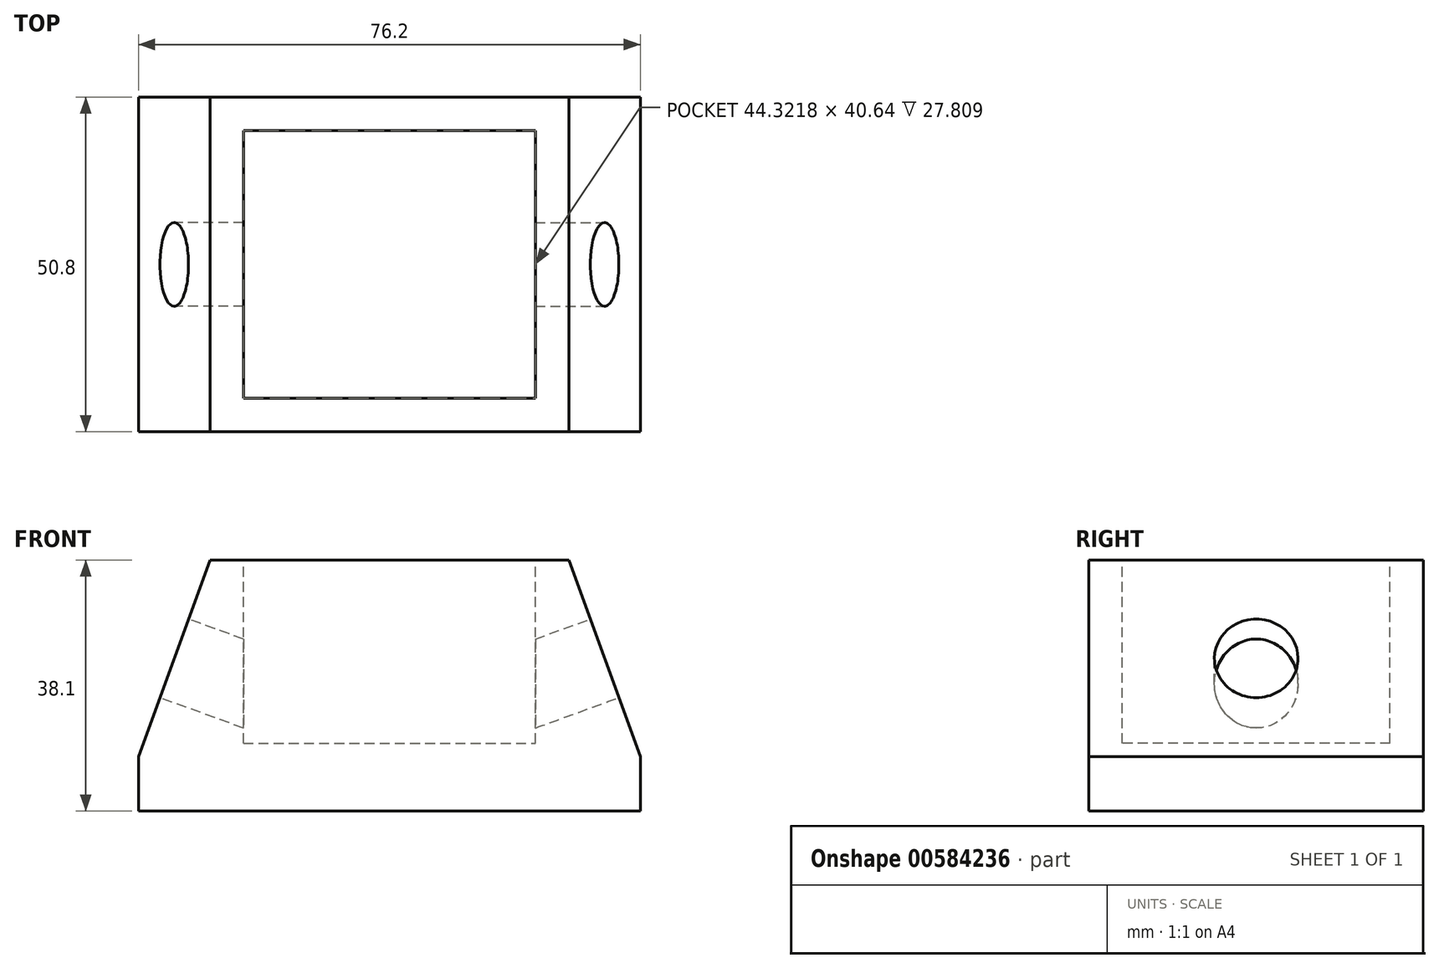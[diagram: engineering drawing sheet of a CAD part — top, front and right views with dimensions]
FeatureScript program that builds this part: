
annotation { "Feature Type Name" : "Feature", "Feature Type Description" : "" }
export const myFeature = defineFeature(function(context is Context, id is Id, definition is map)
    precondition{}
    {
        {
            var Q0;
            Q0=qCreatedBy(makeId("Top.planeOp"),FACE);
            var sketch = newSketch(context, id + "F0", { "sketchPlane" : qUnion([Q0])});
            skLineSegment(sketch, "E0.bottom", {"start": v(0, 0) * mm, "end": v(76.2, 0) * mm});
            skLineSegment(sketch, "E0.top", {"start": v(0, 50.8) * mm, "end": v(76.2, 50.8) * mm});
            skLineSegment(sketch, "E0.left", {"start": v(0, 0) * mm, "end": v(0, 50.8) * mm});
            skLineSegment(sketch, "E0.right", {"start": v(76.2, 0) * mm, "end": v(76.2, 50.8) * mm});
            skSolve(sketch);
        }
        {
            var Q0;
            Q0=makeQuery(id+"F0.imprint","IMPRINT",FACE,{"disambiguationData":[TD([[makeQuery(id+"F0.imprint","IMPRINT",EDGE,{"derivedFrom":sQuery(id+"F0.wireOp",EDGE,"E0.bottom")}),1.0]])]});
            extrude(context, id + "F1", {"entities" : qUnion([Q0]), "depth" : 38.1 * mm, "offsetDistance" : 25.4 * mm});
        }
        {
            var Q0;
            Q0=makeQuery(id+"F1.opExtrude","SWEPT_FACE",FACE,{"disambiguationData":[OSD([sQuery(id+"F0.wireOp",EDGE,"E0.bottom")])]});
            var sketch = newSketch(context, id + "F2", { "sketchPlane" : qUnion([Q0])});
            skLineSegment(sketch, "E1", {"start": v(0, 8.26) * mm, "end": v(10.86, 38.1) * mm});
            skLineSegment(sketch, "E2", {"start": v(38.1, 38.1) * mm, "end": v(38.1, 0) * mm, "construction": true});
            skLineSegment(sketch, "E3.MirrorCS", {"start": v(76.2, 8.26) * mm, "end": v(65.34, 38.1) * mm});
            skLineSegment(sketch, "E4", {"start": v(0, 11.3) * mm, "end": v(76.2, 11.3) * mm, "construction": true});
            skLineSegment(sketch, "E5", {"start": v(5.43, 23.18) * mm, "end": v(38.1, 11.3) * mm, "construction": true});
            skLineSegment(sketch, "E6", {"start": v(0, 10.3) * mm, "end": v(76.2, 10.3) * mm, "construction": true});
            skPoint(sketch, "E7", {"position": v(38.1, 10.3) * mm});
            skSolve(sketch);
        }
        {
            var Q0;
            {var subQ0=sQuery(id+"F2.wireOp",EDGE,"E1");Q0=makeQuery(id+"F2.imprint","IMPRINT",FACE,{"disambiguationData":[TD([[makeQuery(id+"F2.imprint","IMPRINT",EDGE,{"derivedFrom":subQ0}),1.0]])]});}
            var Q1;
            {var subQ0=sQuery(id+"F2.wireOp",EDGE,"E3.MirrorCS");Q1=makeQuery(id+"F2.imprint","IMPRINT",FACE,{"disambiguationData":[TD([[makeQuery(id+"F2.imprint","IMPRINT",EDGE,{"derivedFrom":subQ0}),-1.0]])]});}
            extrude(context, id + "F3", {"entities" : qUnion([Q0, Q1]), "operationType" : NewBodyOperationType.REMOVE, "endBound" : BoundingType.UP_TO_NEXT, "oppositeDirection" : true, "depth" : 25.4 * mm, "offsetDistance" : 25.4 * mm});
        }
        {
            var Q0;
            Q0=makeQuery(id+"F1.opExtrude","CAP_FACE",FACE,{"disambiguationData":[OSD([sQuery(id+"F0.wireOp",EDGE,"E0.bottom"),sQuery(id+"F0.wireOp",EDGE,"E0.top"),sQuery(id+"F0.wireOp",EDGE,"E0.left"),sQuery(id+"F0.wireOp",EDGE,"E0.right")])],"isStart":false});
            var sketch = newSketch(context, id + "F4", { "sketchPlane" : qUnion([Q0])});
            skLineSegment(sketch, "E8.0", {"start": v(15.94, 45.72) * mm, "end": v(15.94, 5.08) * mm});
            skLineSegment(sketch, "E8.1", {"start": v(15.94, 45.72) * mm, "end": v(60.26, 45.72) * mm});
            skLineSegment(sketch, "E8.2", {"start": v(60.26, 45.72) * mm, "end": v(60.26, 5.08) * mm});
            skLineSegment(sketch, "E8.3", {"start": v(15.94, 5.08) * mm, "end": v(60.26, 5.08) * mm});
            skSolve(sketch);
        }
        {
            var Q0;
            Q0=makeQuery(id+"F4.imprint","IMPRINT",FACE,{"disambiguationData":[TD([[makeQuery(id+"F4.imprint","IMPRINT",EDGE,{"derivedFrom":sQuery(id+"F4.wireOp",EDGE,"E8.0")}),1.0]])]});
            var Q1;
            Q1=sQuery(id+"F2.wireOp",VERTEX,"E7");
            extrude(context, id + "F5", {"entities" : qUnion([Q0]), "operationType" : NewBodyOperationType.REMOVE, "endBound" : BoundingType.UP_TO_VERTEX, "oppositeDirection" : true, "depth" : 31.75 * mm, "endBoundEntityVertex" : qUnion([Q1]), "offsetDistance" : 25.4 * mm});
        }
        {
            var Q0;
            Q0=makeQuery(id+"F3.boolean.opBoolean","COPY",FACE,{"derivedFrom":makeQuery(id+"F3.opExtrude","SWEPT_FACE",FACE,{"disambiguationData":[OSD([sQuery(id+"F2.wireOp",EDGE,"E1")])]})});
            var sketch = newSketch(context, id + "F6", { "sketchPlane" : qUnion([Q0])});
            skCircle(sketch, "E9", {"center": v(-25.4, 23.64) * mm, "radius": 6.35 * mm});
            skPoint(sketch, "E9.centerSnap0", {"position": v(-25.4, 39.52) * mm});
            skPoint(sketch, "E9.centerSnap1", {"position": v(-50.8, 23.64) * mm});
            skSolve(sketch);
        }
        {
            var Q0;
            Q0=makeQuery(id+"F6.imprint","IMPRINT",FACE,{"disambiguationData":[TD([[makeQuery(id+"F6.imprint","IMPRINT",EDGE,{"derivedFrom":sQuery(id+"F6.wireOp",EDGE,"E9")}),1.0]])]});
            extrude(context, id + "F7", {"entities" : qUnion([Q0]), "operationType" : NewBodyOperationType.REMOVE, "endBound" : BoundingType.UP_TO_NEXT, "oppositeDirection" : true, "depth" : 25.4 * mm, "offsetDistance" : 25.4 * mm});
        }
        {
            var Q0;
            Q0=makeQuery(id+"F3.boolean.opBoolean","COPY",FACE,{"derivedFrom":makeQuery(id+"F3.opExtrude","SWEPT_FACE",FACE,{"disambiguationData":[OSD([sQuery(id+"F2.wireOp",EDGE,"E3.MirrorCS")])]})});
            var sketch = newSketch(context, id + "F8", { "sketchPlane" : qUnion([Q0])});
            skCircle(sketch, "E10", {"center": v(25.4, -2.42) * mm, "radius": 6.35 * mm});
            skPoint(sketch, "E10.centerSnap0", {"position": v(25.4, 13.45) * mm});
            skPoint(sketch, "E10.centerSnap1", {"position": v(0, -2.42) * mm});
            skSolve(sketch);
        }
        {
            var Q0;
            Q0=makeQuery(id+"F8.imprint","IMPRINT",FACE,{"disambiguationData":[TD([[makeQuery(id+"F8.imprint","IMPRINT",EDGE,{"derivedFrom":sQuery(id+"F8.wireOp",EDGE,"E10")}),1.0]])]});
            extrude(context, id + "F9", {"entities" : qUnion([Q0]), "operationType" : NewBodyOperationType.REMOVE, "endBound" : BoundingType.UP_TO_NEXT, "oppositeDirection" : true, "depth" : 25.4 * mm, "offsetDistance" : 25.4 * mm});
        }
    });
